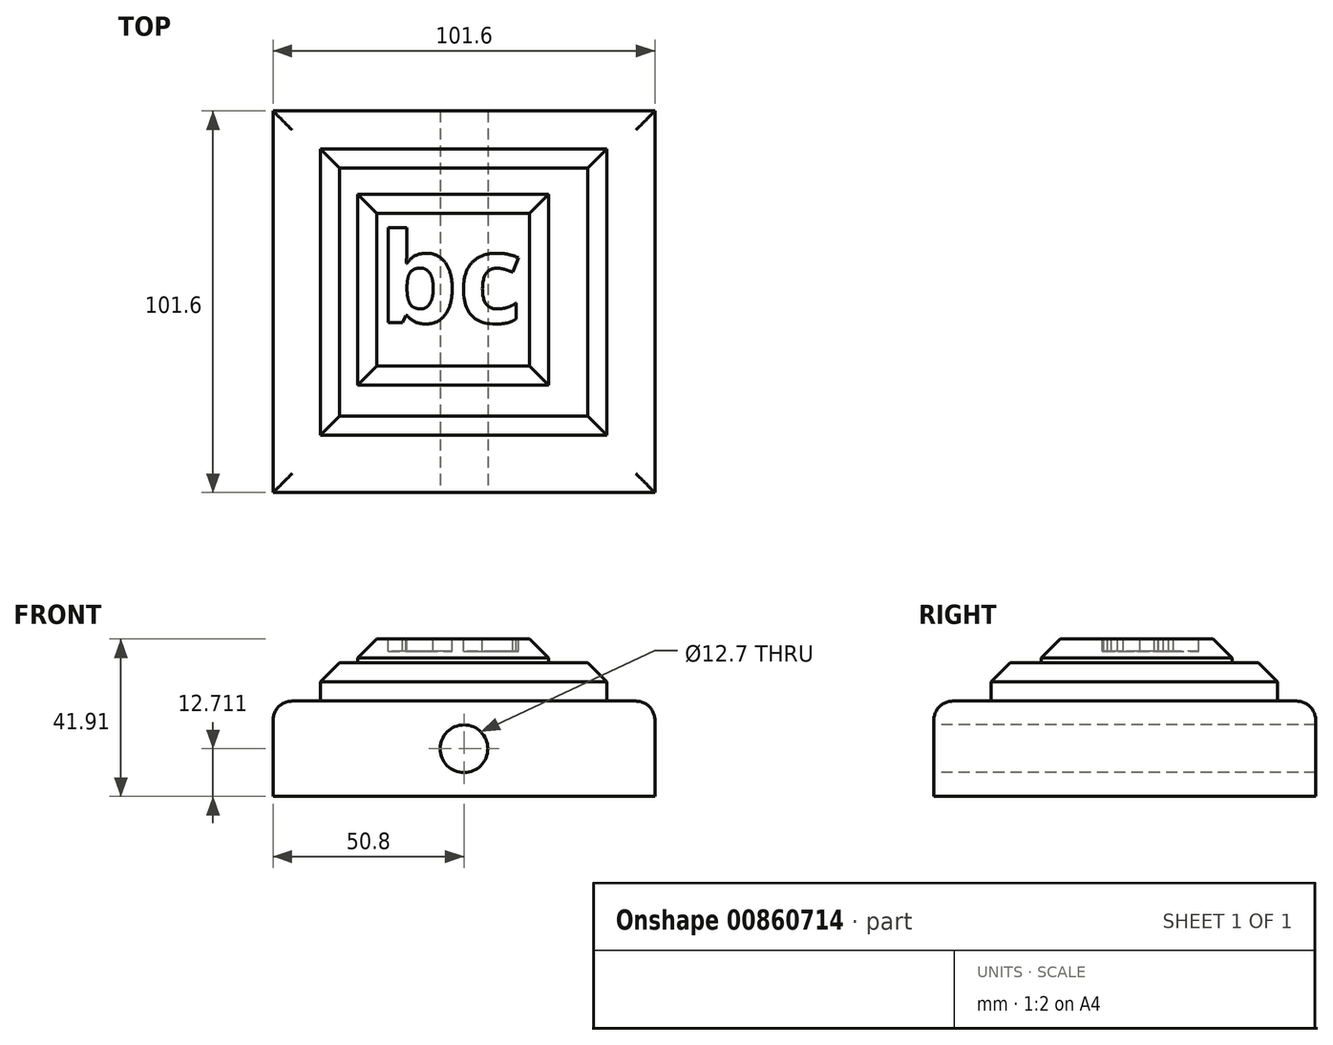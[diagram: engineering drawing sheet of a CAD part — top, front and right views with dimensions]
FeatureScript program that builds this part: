
annotation { "Feature Type Name" : "Feature", "Feature Type Description" : "" }
export const myFeature = defineFeature(function(context is Context, id is Id, definition is map)
    precondition{}
    {
        {
            var Q0;
            Q0=qCreatedBy(makeId("Top.planeOp"),FACE);
            var sketch = newSketch(context, id + "F0", { "sketchPlane" : qUnion([Q0])});
            skLineSegment(sketch, "E0.bottom", {"start": v(-50.8, 101.6) * mm, "end": v(50.8, 101.6) * mm});
            skLineSegment(sketch, "E0.top", {"start": v(-50.8, 0) * mm, "end": v(50.8, 0) * mm});
            skLineSegment(sketch, "E0.left", {"start": v(-50.8, 101.6) * mm, "end": v(-50.8, 0) * mm});
            skLineSegment(sketch, "E0.right", {"start": v(50.8, 101.6) * mm, "end": v(50.8, 0) * mm});
            skSolve(sketch);
        }
        {
            var Q0;
            Q0=makeQuery(id+"F0.imprint","IMPRINT",FACE,{"disambiguationData":[TD([[makeQuery(id+"F0.imprint","IMPRINT",EDGE,{"derivedFrom":sQuery(id+"F0.wireOp",EDGE,"E0.bottom")}),-1.0]])]});
            extrude(context, id + "F1", {"entities" : qUnion([Q0]), "depth" : 25.4 * mm, "offsetDistance" : 25.4 * mm});
        }
        {
            var Q0;
            Q0=makeQuery(id+"F1.opExtrude","CAP_FACE",FACE,{"disambiguationData":[OSD([sQuery(id+"F0.wireOp",EDGE,"E0.bottom"),sQuery(id+"F0.wireOp",EDGE,"E0.top"),sQuery(id+"F0.wireOp",EDGE,"E0.left"),sQuery(id+"F0.wireOp",EDGE,"E0.right")])],"isStart":false});
            var sketch = newSketch(context, id + "F2", { "sketchPlane" : qUnion([Q0])});
            skLineSegment(sketch, "E1.bottom", {"start": v(-38.15, 91.5) * mm, "end": v(38.05, 91.5) * mm});
            skLineSegment(sketch, "E1.top", {"start": v(-38.15, 15.3) * mm, "end": v(38.05, 15.3) * mm});
            skLineSegment(sketch, "E1.left", {"start": v(-38.15, 91.5) * mm, "end": v(-38.15, 15.3) * mm});
            skLineSegment(sketch, "E1.right", {"start": v(38.05, 91.5) * mm, "end": v(38.05, 15.3) * mm});
            skSolve(sketch);
        }
        {
            var Q0;
            Q0=makeQuery(id+"F2.imprint","IMPRINT",FACE,{"disambiguationData":[TD([[makeQuery(id+"F2.imprint","IMPRINT",EDGE,{"derivedFrom":sQuery(id+"F2.wireOp",EDGE,"E1.bottom")}),-1.0]])]});
            extrude(context, id + "F3", {"entities" : qUnion([Q0]), "operationType" : NewBodyOperationType.ADD, "depth" : 10.16 * mm, "offsetDistance" : 25.4 * mm});
        }
        {
            var Q0;
            Q0=makeQuery(id+"F3.opExtrude","CAP_FACE",FACE,{"disambiguationData":[OSD([sQuery(id+"F2.wireOp",EDGE,"E1.bottom"),sQuery(id+"F2.wireOp",EDGE,"E1.top"),sQuery(id+"F2.wireOp",EDGE,"E1.left"),sQuery(id+"F2.wireOp",EDGE,"E1.right")])],"isStart":false});
            var sketch = newSketch(context, id + "F4", { "sketchPlane" : qUnion([Q0])});
            skLineSegment(sketch, "E2.bottom", {"start": v(-28.33, 79.41) * mm, "end": v(22.47, 79.41) * mm});
            skLineSegment(sketch, "E2.top", {"start": v(-28.33, 28.61) * mm, "end": v(22.47, 28.61) * mm});
            skLineSegment(sketch, "E2.left", {"start": v(-28.33, 79.41) * mm, "end": v(-28.33, 28.61) * mm});
            skLineSegment(sketch, "E2.right", {"start": v(22.47, 79.41) * mm, "end": v(22.47, 28.61) * mm});
            skSolve(sketch);
        }
        {
            var Q0;
            Q0=makeQuery(id+"F4.imprint","IMPRINT",FACE,{"disambiguationData":[TD([[makeQuery(id+"F4.imprint","IMPRINT",EDGE,{"derivedFrom":sQuery(id+"F4.wireOp",EDGE,"E2.bottom")}),-1.0]])]});
            extrude(context, id + "F5", {"entities" : qUnion([Q0]), "operationType" : NewBodyOperationType.ADD, "depth" : 6.35 * mm, "offsetDistance" : 25.4 * mm});
        }
        {
            var Q0;
            Q0=makeQuery(id+"F5.opExtrude","CAP_FACE",FACE,{"disambiguationData":[OSD([sQuery(id+"F4.wireOp",EDGE,"E2.bottom"),sQuery(id+"F4.wireOp",EDGE,"E2.top"),sQuery(id+"F4.wireOp",EDGE,"E2.left"),sQuery(id+"F4.wireOp",EDGE,"E2.right")])],"isStart":false});
            var sketch = newSketch(context, id + "F6", { "sketchPlane" : qUnion([Q0])});
            skText(sketch, "E3", { "text": "bc", "fontName": "OpenSans-Bold.ttf"});
            const initialGuessF6  = {"E3": [-0.02273, 0.0452, 1, 0, 0.024]};
            skSetInitialGuess(sketch, initialGuessF6);
            skSolve(sketch);
        }
        {
            var Q0;
            Q0 = qSketchRegion(id + "F6", true);
            extrude(context, id + "F7", {"entities" : qUnion([Q0]), "operationType" : NewBodyOperationType.REMOVE, "oppositeDirection" : true, "depth" : 3.3 * mm, "offsetDistance" : 25.4 * mm});
        }
        {
            var Q0;
            Q0=makeQuery(id+"F1.opExtrude","SWEPT_FACE",FACE,{"disambiguationData":[OSD([sQuery(id+"F0.wireOp",EDGE,"E0.top")])]});
            var sketch = newSketch(context, id + "F8", { "sketchPlane" : qUnion([Q0])});
            skCircle(sketch, "E4", {"center": v(0, 12.71) * mm, "radius": 6.35 * mm});
            skSolve(sketch);
        }
        {
            var Q0;
            Q0 = qSketchRegion(id + "F8", true);
            extrude(context, id + "F9", {"entities" : qUnion([Q0]), "operationType" : NewBodyOperationType.REMOVE, "oppositeDirection" : true, "depth" : 122.68 * mm, "offsetDistance" : 25.4 * mm});
        }
        {
            var Q0;
            Q0=makeQuery(id+"F1.opExtrude","CAP_EDGE",EDGE,{"disambiguationData":[OSD([sQuery(id+"F0.wireOp",EDGE,"E0.left")])],"isStart":false});
            var Q1;
            Q1=makeQuery(id+"F1.opExtrude","CAP_EDGE",EDGE,{"disambiguationData":[OSD([sQuery(id+"F0.wireOp",EDGE,"E0.bottom")])],"isStart":false});
            var Q2;
            Q2=makeQuery(id+"F1.opExtrude","CAP_EDGE",EDGE,{"disambiguationData":[OSD([sQuery(id+"F0.wireOp",EDGE,"E0.right")])],"isStart":false});
            var Q3;
            Q3=makeQuery(id+"F1.opExtrude","CAP_EDGE",EDGE,{"disambiguationData":[OSD([sQuery(id+"F0.wireOp",EDGE,"E0.top")])],"isStart":false});
            fillet(context, id + "F10", {"entities" : qUnion([Q0, Q1, Q2, Q3]), "radius" : 5.08 * mm, "tangentPropagation" : true, "allowEdgeOverflow" : false});
        }
        {
            var Q0;
            Q0=makeQuery(id+"F3.opExtrude","CAP_EDGE",EDGE,{"disambiguationData":[OSD([sQuery(id+"F2.wireOp",EDGE,"E1.bottom")])],"isStart":false});
            var Q1;
            Q1=makeQuery(id+"F3.opExtrude","CAP_EDGE",EDGE,{"disambiguationData":[OSD([sQuery(id+"F2.wireOp",EDGE,"E1.right")])],"isStart":false});
            var Q2;
            Q2=makeQuery(id+"F3.opExtrude","CAP_EDGE",EDGE,{"disambiguationData":[OSD([sQuery(id+"F2.wireOp",EDGE,"E1.top")])],"isStart":false});
            var Q3;
            Q3=makeQuery(id+"F3.opExtrude","CAP_EDGE",EDGE,{"disambiguationData":[OSD([sQuery(id+"F2.wireOp",EDGE,"E1.left")])],"isStart":false});
            chamfer(context, id + "F11", {"entities" : qUnion([Q0, Q1, Q2, Q3]), "width" : 5.08 * mm, "tangentPropagation" : true});
        }
        {
            var Q0;
            Q0=makeQuery(id+"F5.opExtrude","CAP_EDGE",EDGE,{"disambiguationData":[OSD([sQuery(id+"F4.wireOp",EDGE,"E2.bottom")])],"isStart":false});
            var Q1;
            Q1=makeQuery(id+"F5.opExtrude","CAP_EDGE",EDGE,{"disambiguationData":[OSD([sQuery(id+"F4.wireOp",EDGE,"E2.left")])],"isStart":false});
            var Q2;
            Q2=makeQuery(id+"F5.opExtrude","CAP_EDGE",EDGE,{"disambiguationData":[OSD([sQuery(id+"F4.wireOp",EDGE,"E2.top")])],"isStart":false});
            var Q3;
            Q3=makeQuery(id+"F5.opExtrude","CAP_EDGE",EDGE,{"disambiguationData":[OSD([sQuery(id+"F4.wireOp",EDGE,"E2.right")])],"isStart":false});
            chamfer(context, id + "F12", {"entities" : qUnion([Q0, Q1, Q2, Q3]), "width" : 5.08 * mm, "tangentPropagation" : true});
        }
    });
